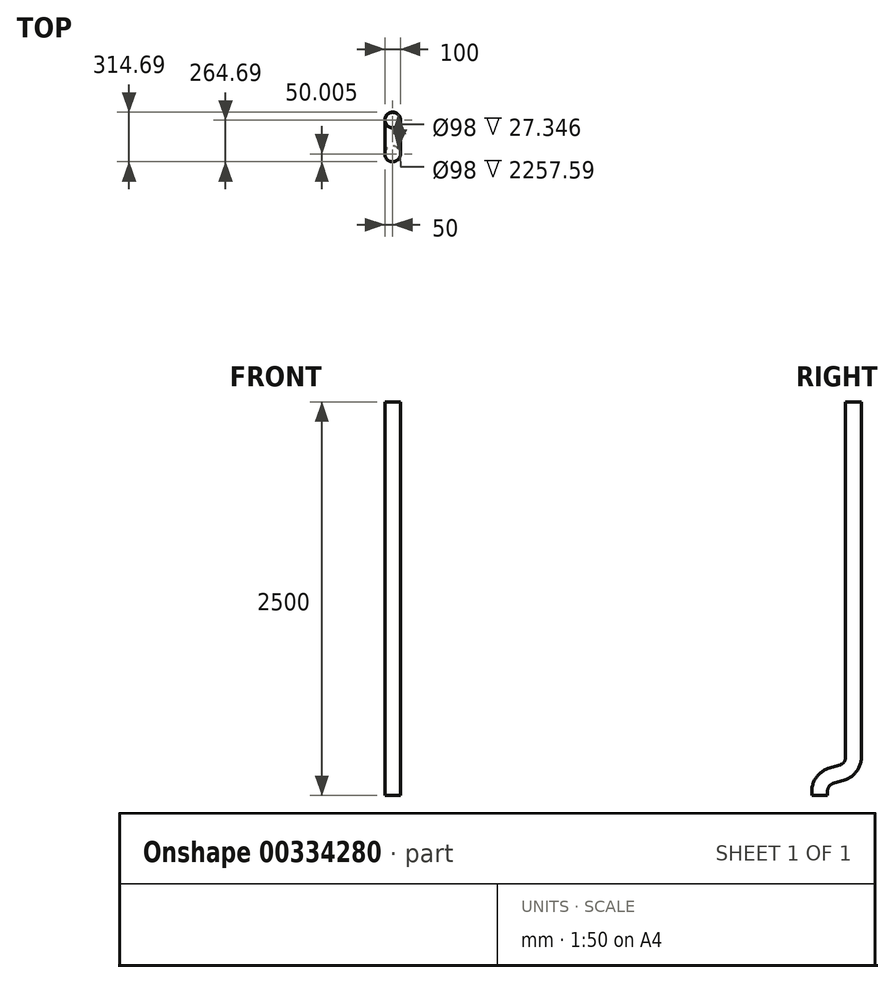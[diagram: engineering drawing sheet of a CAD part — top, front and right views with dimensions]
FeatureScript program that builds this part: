
annotation { "Feature Type Name" : "Feature", "Feature Type Description" : "" }
export const myFeature = defineFeature(function(context is Context, id is Id, definition is map)
    precondition{}
    {
        {
            var Q0;
            Q0=qCreatedBy(makeId("Right.planeOp"),FACE);
            var sketch = newSketch(context, id + "F0", { "sketchPlane" : qUnion([Q0])});
            skLineSegment(sketch, "E0", {"start": v(0, 0) * mm, "end": v(0, -2257.6) * mm});
            skLineSegment(sketch, "E1", {"start": v(-69.1, -2352.7) * mm, "end": v(-145.59, -2377.55) * mm});
            skLineSegment(sketch, "E2", {"start": v(-214.68, -2472.65) * mm, "end": v(-214.68, -2500) * mm});
            skPoint(sketch, "E3.visualSharp", {"position": v(0, -2330.24) * mm});
            skArc(sketch, "E3.filletArc", {"start": v(-69.1, -2352.7) * mm, "mid": v(-19.1, -2316.37) * mm, "end": v(0, -2257.6) * mm});
            skPoint(sketch, "E4.visualSharp", {"position": v(-214.68, -2400) * mm});
            skArc(sketch, "E4.filletArc", {"start": v(-145.59, -2377.55) * mm, "mid": v(-195.59, -2413.88) * mm, "end": v(-214.68, -2472.65) * mm});
            skSolve(sketch);
        }
        {
            var Q0;
            Q0=qCreatedBy(makeId("Top.planeOp"),FACE);
            var sketch = newSketch(context, id + "F1", { "sketchPlane" : qUnion([Q0])});
            skCircle(sketch, "E5", {"center": v(0, 0) * mm, "radius": 50 * mm});
            skCircle(sketch, "E6", {"center": v(0, 0) * mm, "radius": 49 * mm});
            skSolve(sketch);
        }
        {
            var Q0;
            Q0=makeQuery(id+"F1.imprint","IMPRINT",FACE,{"disambiguationData":[TD([[makeQuery(id+"F1.imprint","IMPRINT",EDGE,{"derivedFrom":sQuery(id+"F1.wireOp",EDGE,"E5")}),1.0]])]});
            var Q1;
            Q1=sQuery(id+"F0.wireOp",EDGE,"E0");
            var Q2;
            Q2=sQuery(id+"F0.wireOp",EDGE,"E3.filletArc");
            var Q3;
            Q3=sQuery(id+"F0.wireOp",EDGE,"E1");
            var Q4;
            Q4=sQuery(id+"F0.wireOp",EDGE,"E4.filletArc");
            var Q5;
            Q5=sQuery(id+"F0.wireOp",EDGE,"E2");
            sweep(context, id + "F2", {"profiles" : qUnion([Q0]), "path" : qUnion([Q1, Q2, Q3, Q4, Q5])});
        }
    });
